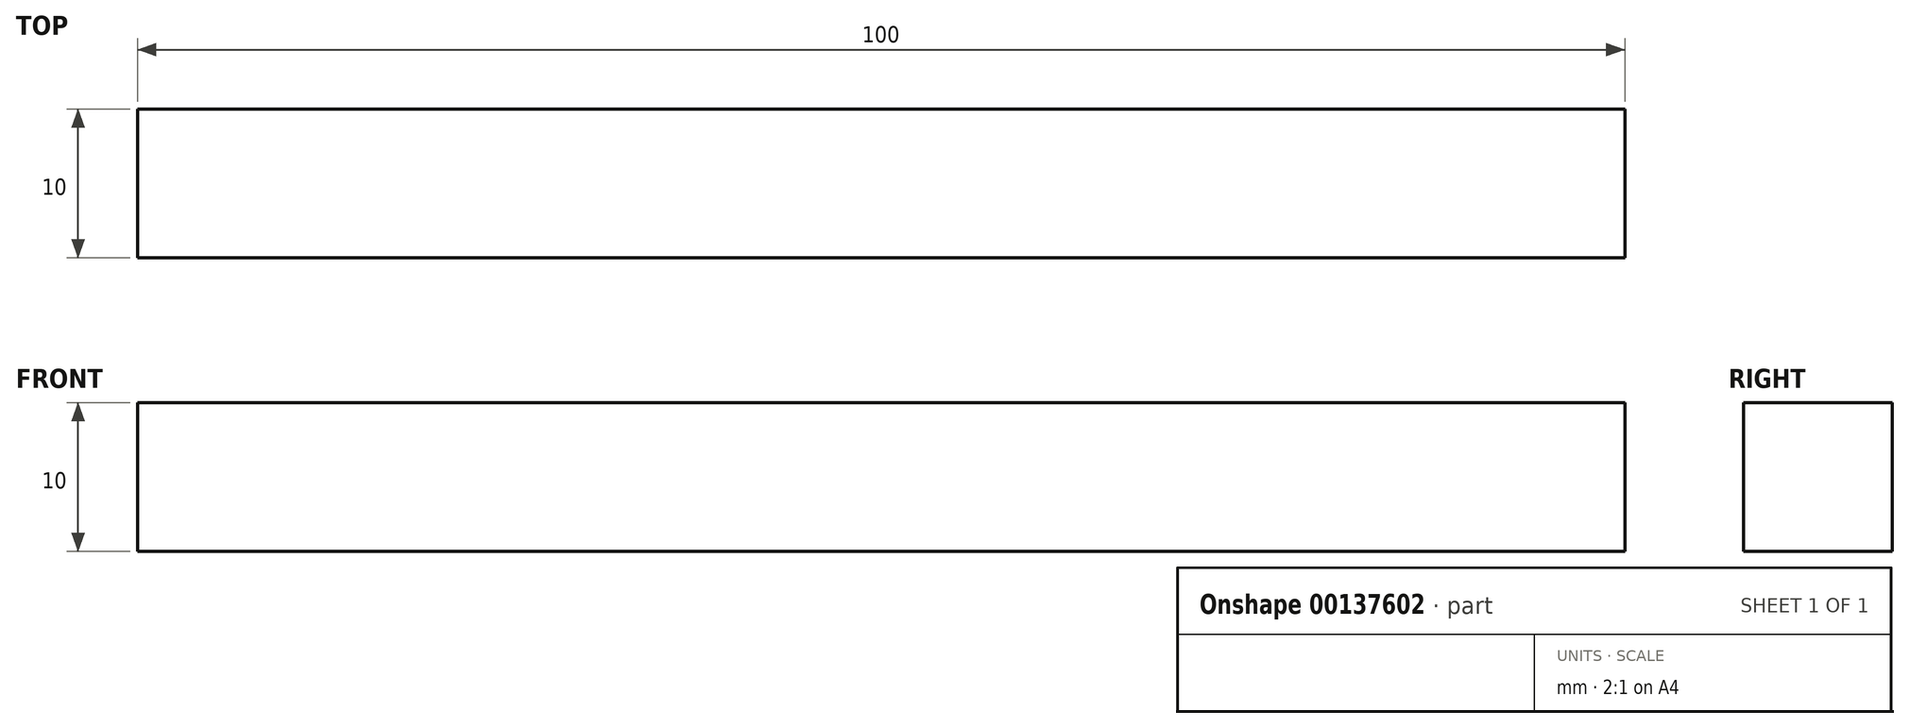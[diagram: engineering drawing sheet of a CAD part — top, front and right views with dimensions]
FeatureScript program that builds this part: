
annotation { "Feature Type Name" : "Feature", "Feature Type Description" : "" }
export const myFeature = defineFeature(function(context is Context, id is Id, definition is map)
    precondition{}
    {
        {
            var Q0;
            Q0=qCreatedBy(makeId("Top.planeOp"),FACE);
            var sketch = newSketch(context, id + "F0", { "sketchPlane" : qUnion([Q0])});
            skLineSegment(sketch, "E0.bottom", {"start": v(0, 0) * mm, "end": v(100, 0) * mm});
            skLineSegment(sketch, "E0.top", {"start": v(0, 10) * mm, "end": v(100, 10) * mm});
            skLineSegment(sketch, "E0.left", {"start": v(0, 0) * mm, "end": v(0, 10) * mm});
            skLineSegment(sketch, "E0.right", {"start": v(100, 0) * mm, "end": v(100, 10) * mm});
            skSolve(sketch);
        }
        {
            var Q0;
            Q0 = qSketchRegion(id + "F0", true);
            extrude(context, id + "F1", {"entities" : qUnion([Q0]), "depth" : 10 * mm});
        }
    });
